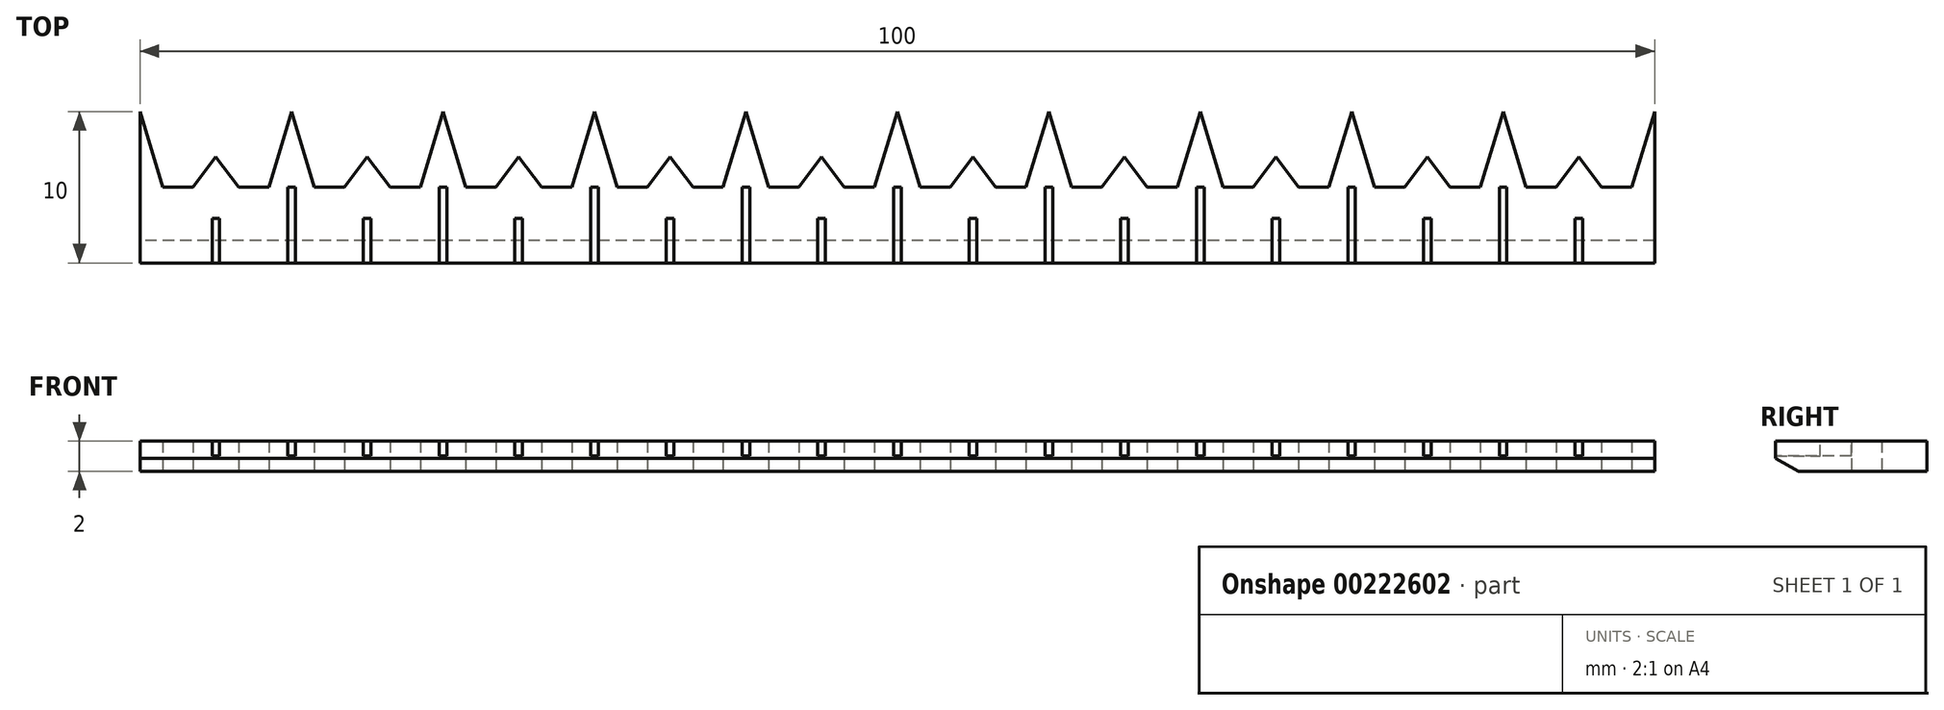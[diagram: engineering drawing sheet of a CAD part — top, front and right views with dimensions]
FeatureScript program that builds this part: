
annotation { "Feature Type Name" : "Feature", "Feature Type Description" : "" }
export const myFeature = defineFeature(function(context is Context, id is Id, definition is map)
    precondition{}
    {
        {
            var Q0;
            Q0=qCreatedBy(makeId("Top.planeOp"),FACE);
            var sketch = newSketch(context, id + "F0", { "sketchPlane" : qUnion([Q0])});
            skLineSegment(sketch, "E0.bottom", {"start": v(50, -2.5) * mm, "end": v(-50, -2.5) * mm});
            skLineSegment(sketch, "E0.top", {"start": v(50, 2.5) * mm, "end": v(-50, 2.5) * mm});
            skLineSegment(sketch, "E0.left", {"start": v(50, -2.5) * mm, "end": v(50, 2.5) * mm});
            skLineSegment(sketch, "E0.right", {"start": v(-50, -2.5) * mm, "end": v(-50, 2.5) * mm});
            skPoint(sketch, "E0.middle", {"position": v(0, 0) * mm});
            skLineSegment(sketch, "E1", {"start": v(-40, -2.5) * mm, "end": v(-40, 23.77) * mm, "construction": true});
            skLineSegment(sketch, "E2", {"start": v(-41.5, 2.5) * mm, "end": v(-40, 7.5) * mm});
            skLineSegment(sketch, "E3.MirrorCS", {"start": v(-38.5, 2.5) * mm, "end": v(-40, 7.5) * mm});
            skLineSegment(sketch, "E4.1.0.0", {"start": v(-31.5, 2.5) * mm, "end": v(-30, 7.5) * mm});
            skLineSegment(sketch, "E4.1.0.1", {"start": v(-28.5, 2.5) * mm, "end": v(-30, 7.5) * mm});
            skLineSegment(sketch, "E4.2.0.0", {"start": v(-21.5, 2.5) * mm, "end": v(-20, 7.5) * mm});
            skLineSegment(sketch, "E4.2.0.1", {"start": v(-18.5, 2.5) * mm, "end": v(-20, 7.5) * mm});
            skLineSegment(sketch, "E4.3.0.0", {"start": v(-11.5, 2.5) * mm, "end": v(-10, 7.5) * mm});
            skLineSegment(sketch, "E4.3.0.1", {"start": v(-8.5, 2.5) * mm, "end": v(-10, 7.5) * mm});
            skLineSegment(sketch, "E4.4.0.0", {"start": v(-1.5, 2.5) * mm, "end": v(0, 7.5) * mm});
            skLineSegment(sketch, "E4.4.0.1", {"start": v(1.5, 2.5) * mm, "end": v(0, 7.5) * mm});
            skLineSegment(sketch, "E4.5.0.0", {"start": v(8.5, 2.5) * mm, "end": v(10, 7.5) * mm});
            skLineSegment(sketch, "E4.5.0.1", {"start": v(11.5, 2.5) * mm, "end": v(10, 7.5) * mm});
            skLineSegment(sketch, "E4.6.0.0", {"start": v(18.5, 2.5) * mm, "end": v(20, 7.5) * mm});
            skLineSegment(sketch, "E4.6.0.1", {"start": v(21.5, 2.5) * mm, "end": v(20, 7.5) * mm});
            skLineSegment(sketch, "E4.7.0.0", {"start": v(28.5, 2.5) * mm, "end": v(30, 7.5) * mm});
            skLineSegment(sketch, "E4.7.0.1", {"start": v(31.5, 2.5) * mm, "end": v(30, 7.5) * mm});
            skLineSegment(sketch, "E4.8.0.0", {"start": v(38.5, 2.5) * mm, "end": v(40, 7.5) * mm});
            skLineSegment(sketch, "E4.8.0.1", {"start": v(41.5, 2.5) * mm, "end": v(40, 7.5) * mm});
            skLineSegment(sketch, "E4.direction1", {"start": v(-41.5, 2.5) * mm, "end": v(-31.5, 2.5) * mm, "construction": true});
            skLineSegment(sketch, "E5", {"start": v(-48.5, 2.5) * mm, "end": v(-50, 7.5) * mm});
            skLineSegment(sketch, "E6", {"start": v(-50, 7.5) * mm, "end": v(-50, 2.5) * mm});
            skLineSegment(sketch, "E7", {"start": v(48.5, 2.5) * mm, "end": v(50, 7.5) * mm});
            skLineSegment(sketch, "E8", {"start": v(-50, 2.5) * mm, "end": v(-48.5, 2.5) * mm});
            skLineSegment(sketch, "E9", {"start": v(48.5, 2.5) * mm, "end": v(50, 2.5) * mm});
            skLineSegment(sketch, "E10", {"start": v(50, 7.5) * mm, "end": v(50, 2.5) * mm});
            skLineSegment(sketch, "E11", {"start": v(-41.5, 2.5) * mm, "end": v(-40, 2.5) * mm});
            skLineSegment(sketch, "E12", {"start": v(-45, -2.5) * mm, "end": v(-45, 6.78) * mm, "construction": true});
            skLineSegment(sketch, "E13", {"start": v(-46.5, 2.5) * mm, "end": v(-45, 4.5) * mm});
            skLineSegment(sketch, "E14.MirrorCS", {"start": v(-43.5, 2.5) * mm, "end": v(-45, 4.5) * mm});
            skLineSegment(sketch, "E15", {"start": v(-46.5, 2.5) * mm, "end": v(-43.5, 2.5) * mm});
            skLineSegment(sketch, "E16", {"start": v(-41.5, 2.5) * mm, "end": v(-38.5, 2.5) * mm});
            skLineSegment(sketch, "E17.1.0.0", {"start": v(-33.5, 2.5) * mm, "end": v(-35, 4.5) * mm});
            skLineSegment(sketch, "E17.1.0.1", {"start": v(-36.5, 2.5) * mm, "end": v(-35, 4.5) * mm});
            skLineSegment(sketch, "E17.1.0.2", {"start": v(-36.5, 2.5) * mm, "end": v(-33.5, 2.5) * mm});
            skLineSegment(sketch, "E17.2.0.0", {"start": v(-23.5, 2.5) * mm, "end": v(-25, 4.5) * mm});
            skLineSegment(sketch, "E17.2.0.1", {"start": v(-26.5, 2.5) * mm, "end": v(-25, 4.5) * mm});
            skLineSegment(sketch, "E17.2.0.2", {"start": v(-26.5, 2.5) * mm, "end": v(-23.5, 2.5) * mm});
            skLineSegment(sketch, "E17.3.0.0", {"start": v(-13.5, 2.5) * mm, "end": v(-15, 4.5) * mm});
            skLineSegment(sketch, "E17.3.0.1", {"start": v(-16.5, 2.5) * mm, "end": v(-15, 4.5) * mm});
            skLineSegment(sketch, "E17.3.0.2", {"start": v(-16.5, 2.5) * mm, "end": v(-13.5, 2.5) * mm});
            skLineSegment(sketch, "E17.4.0.0", {"start": v(-3.5, 2.5) * mm, "end": v(-5, 4.5) * mm});
            skLineSegment(sketch, "E17.4.0.1", {"start": v(-6.5, 2.5) * mm, "end": v(-5, 4.5) * mm});
            skLineSegment(sketch, "E17.4.0.2", {"start": v(-6.5, 2.5) * mm, "end": v(-3.5, 2.5) * mm});
            skLineSegment(sketch, "E17.5.0.0", {"start": v(6.5, 2.5) * mm, "end": v(5, 4.5) * mm});
            skLineSegment(sketch, "E17.5.0.1", {"start": v(3.5, 2.5) * mm, "end": v(5, 4.5) * mm});
            skLineSegment(sketch, "E17.5.0.2", {"start": v(3.5, 2.5) * mm, "end": v(6.5, 2.5) * mm});
            skLineSegment(sketch, "E17.6.0.0", {"start": v(16.5, 2.5) * mm, "end": v(15, 4.5) * mm});
            skLineSegment(sketch, "E17.6.0.1", {"start": v(13.5, 2.5) * mm, "end": v(15, 4.5) * mm});
            skLineSegment(sketch, "E17.6.0.2", {"start": v(13.5, 2.5) * mm, "end": v(16.5, 2.5) * mm});
            skLineSegment(sketch, "E17.7.0.0", {"start": v(26.5, 2.5) * mm, "end": v(25, 4.5) * mm});
            skLineSegment(sketch, "E17.7.0.1", {"start": v(23.5, 2.5) * mm, "end": v(25, 4.5) * mm});
            skLineSegment(sketch, "E17.7.0.2", {"start": v(23.5, 2.5) * mm, "end": v(26.5, 2.5) * mm});
            skLineSegment(sketch, "E17.8.0.0", {"start": v(36.5, 2.5) * mm, "end": v(35, 4.5) * mm});
            skLineSegment(sketch, "E17.8.0.1", {"start": v(33.5, 2.5) * mm, "end": v(35, 4.5) * mm});
            skLineSegment(sketch, "E17.8.0.2", {"start": v(33.5, 2.5) * mm, "end": v(36.5, 2.5) * mm});
            skLineSegment(sketch, "E17.9.0.0", {"start": v(46.5, 2.5) * mm, "end": v(45, 4.5) * mm});
            skLineSegment(sketch, "E17.9.0.1", {"start": v(43.5, 2.5) * mm, "end": v(45, 4.5) * mm});
            skLineSegment(sketch, "E17.9.0.2", {"start": v(43.5, 2.5) * mm, "end": v(46.5, 2.5) * mm});
            skLineSegment(sketch, "E17.direction1", {"start": v(-46.5, 2.5) * mm, "end": v(-36.5, 2.5) * mm, "construction": true});
            skSolve(sketch);
        }
        {
            var Q0;
            Q0 = qSketchRegion(id + "F0", true);
            extrude(context, id + "F1", {"entities" : qUnion([Q0]), "depth" : 2 * mm});
        }
        {
            var Q0;
            Q0=makeQuery(id+"F1.opExtrude","CAP_EDGE",EDGE,{"disambiguationData":[OSD([sQuery(id+"F0.wireOp",EDGE,"E0.bottom")])],"isStart":true});
            chamfer(context, id + "F2", {"entities" : qUnion([Q0]), "chamferType" : ChamferType.OFFSET_ANGLE, "width" : 1.5 * mm, "oppositeDirection" : false, "angle" : 30 * degree, "tangentPropagation" : true});
        }
        {
            var Q0;
            Q0=makeQuery(id+"F1.opExtrude","CAP_FACE",FACE,{"disambiguationData":[OSD([sQuery(id+"F0.wireOp",EDGE,"E0.bottom"),sQuery(id+"F0.wireOp",EDGE,"E0.top"),sQuery(id+"F0.wireOp",EDGE,"E0.left"),sQuery(id+"F0.wireOp",EDGE,"E0.right"),sQuery(id+"F0.wireOp",EDGE,"E2"),sQuery(id+"F0.wireOp",EDGE,"E3.MirrorCS"),sQuery(id+"F0.wireOp",EDGE,"E4.1.0.0"),sQuery(id+"F0.wireOp",EDGE,"E4.1.0.1"),sQuery(id+"F0.wireOp",EDGE,"E4.2.0.0"),sQuery(id+"F0.wireOp",EDGE,"E4.2.0.1"),sQuery(id+"F0.wireOp",EDGE,"E4.3.0.0"),sQuery(id+"F0.wireOp",EDGE,"E4.3.0.1"),sQuery(id+"F0.wireOp",EDGE,"E4.4.0.0"),sQuery(id+"F0.wireOp",EDGE,"E4.4.0.1"),sQuery(id+"F0.wireOp",EDGE,"E4.5.0.0"),sQuery(id+"F0.wireOp",EDGE,"E4.5.0.1"),sQuery(id+"F0.wireOp",EDGE,"E4.6.0.0"),sQuery(id+"F0.wireOp",EDGE,"E4.6.0.1"),sQuery(id+"F0.wireOp",EDGE,"E4.7.0.0"),sQuery(id+"F0.wireOp",EDGE,"E4.7.0.1"),sQuery(id+"F0.wireOp",EDGE,"E4.8.0.0"),sQuery(id+"F0.wireOp",EDGE,"E4.8.0.1"),sQuery(id+"F0.wireOp",EDGE,"E5"),sQuery(id+"F0.wireOp",EDGE,"E6"),sQuery(id+"F0.wireOp",EDGE,"E7"),sQuery(id+"F0.wireOp",EDGE,"E10"),sQuery(id+"F0.wireOp",EDGE,"E13"),sQuery(id+"F0.wireOp",EDGE,"E14.MirrorCS"),sQuery(id+"F0.wireOp",EDGE,"E17.1.0.0"),sQuery(id+"F0.wireOp",EDGE,"E17.1.0.1"),sQuery(id+"F0.wireOp",EDGE,"E17.2.0.0"),sQuery(id+"F0.wireOp",EDGE,"E17.2.0.1"),sQuery(id+"F0.wireOp",EDGE,"E17.3.0.0"),sQuery(id+"F0.wireOp",EDGE,"E17.3.0.1"),sQuery(id+"F0.wireOp",EDGE,"E17.4.0.0"),sQuery(id+"F0.wireOp",EDGE,"E17.4.0.1"),sQuery(id+"F0.wireOp",EDGE,"E17.5.0.0"),sQuery(id+"F0.wireOp",EDGE,"E17.5.0.1"),sQuery(id+"F0.wireOp",EDGE,"E17.6.0.0"),sQuery(id+"F0.wireOp",EDGE,"E17.6.0.1"),sQuery(id+"F0.wireOp",EDGE,"E17.7.0.0"),sQuery(id+"F0.wireOp",EDGE,"E17.7.0.1"),sQuery(id+"F0.wireOp",EDGE,"E17.8.0.0"),sQuery(id+"F0.wireOp",EDGE,"E17.8.0.1"),sQuery(id+"F0.wireOp",EDGE,"E17.9.0.0"),sQuery(id+"F0.wireOp",EDGE,"E17.9.0.1")])],"isStart":false});
            var sketch = newSketch(context, id + "F3", { "sketchPlane" : qUnion([Q0])});
            skLineSegment(sketch, "E18.bottom", {"start": v(-39.75, 2.5) * mm, "end": v(-40.25, 2.5) * mm});
            skLineSegment(sketch, "E18.top", {"start": v(-39.75, -2.5) * mm, "end": v(-40.25, -2.5) * mm});
            skLineSegment(sketch, "E18.left", {"start": v(-39.75, 2.5) * mm, "end": v(-39.75, -2.5) * mm});
            skLineSegment(sketch, "E18.right", {"start": v(-40.25, 2.5) * mm, "end": v(-40.25, -2.5) * mm});
            skPoint(sketch, "E18.middle", {"position": v(-40, 0) * mm});
            skLineSegment(sketch, "E19.1.0.0", {"start": v(-29.75, 2.5) * mm, "end": v(-29.75, -2.5) * mm});
            skLineSegment(sketch, "E19.1.0.1", {"start": v(-30.25, 2.5) * mm, "end": v(-30.25, -2.5) * mm});
            skPoint(sketch, "E19.1.0.2", {"position": v(-30, 0) * mm});
            skLineSegment(sketch, "E19.1.0.3", {"start": v(-29.75, 2.5) * mm, "end": v(-30.25, 2.5) * mm});
            skLineSegment(sketch, "E19.1.0.4", {"start": v(-29.75, -2.5) * mm, "end": v(-30.25, -2.5) * mm});
            skLineSegment(sketch, "E19.2.0.0", {"start": v(-19.75, 2.5) * mm, "end": v(-19.75, -2.5) * mm});
            skLineSegment(sketch, "E19.2.0.1", {"start": v(-20.25, 2.5) * mm, "end": v(-20.25, -2.5) * mm});
            skPoint(sketch, "E19.2.0.2", {"position": v(-20, 0) * mm});
            skLineSegment(sketch, "E19.2.0.3", {"start": v(-19.75, 2.5) * mm, "end": v(-20.25, 2.5) * mm});
            skLineSegment(sketch, "E19.2.0.4", {"start": v(-19.75, -2.5) * mm, "end": v(-20.25, -2.5) * mm});
            skLineSegment(sketch, "E19.3.0.0", {"start": v(-9.75, 2.5) * mm, "end": v(-9.75, -2.5) * mm});
            skLineSegment(sketch, "E19.3.0.1", {"start": v(-10.25, 2.5) * mm, "end": v(-10.25, -2.5) * mm});
            skPoint(sketch, "E19.3.0.2", {"position": v(-10, 0) * mm});
            skLineSegment(sketch, "E19.3.0.3", {"start": v(-9.75, 2.5) * mm, "end": v(-10.25, 2.5) * mm});
            skLineSegment(sketch, "E19.3.0.4", {"start": v(-9.75, -2.5) * mm, "end": v(-10.25, -2.5) * mm});
            skLineSegment(sketch, "E19.4.0.0", {"start": v(0.25, 2.5) * mm, "end": v(0.25, -2.5) * mm});
            skLineSegment(sketch, "E19.4.0.1", {"start": v(-0.25, 2.5) * mm, "end": v(-0.25, -2.5) * mm});
            skPoint(sketch, "E19.4.0.2", {"position": v(0, 0) * mm});
            skLineSegment(sketch, "E19.4.0.3", {"start": v(0.25, 2.5) * mm, "end": v(-0.25, 2.5) * mm});
            skLineSegment(sketch, "E19.4.0.4", {"start": v(0.25, -2.5) * mm, "end": v(-0.25, -2.5) * mm});
            skLineSegment(sketch, "E19.5.0.0", {"start": v(10.25, 2.5) * mm, "end": v(10.25, -2.5) * mm});
            skLineSegment(sketch, "E19.5.0.1", {"start": v(9.75, 2.5) * mm, "end": v(9.75, -2.5) * mm});
            skPoint(sketch, "E19.5.0.2", {"position": v(10, 0) * mm});
            skLineSegment(sketch, "E19.5.0.3", {"start": v(10.25, 2.5) * mm, "end": v(9.75, 2.5) * mm});
            skLineSegment(sketch, "E19.5.0.4", {"start": v(10.25, -2.5) * mm, "end": v(9.75, -2.5) * mm});
            skLineSegment(sketch, "E19.6.0.0", {"start": v(20.25, 2.5) * mm, "end": v(20.25, -2.5) * mm});
            skLineSegment(sketch, "E19.6.0.1", {"start": v(19.75, 2.5) * mm, "end": v(19.75, -2.5) * mm});
            skPoint(sketch, "E19.6.0.2", {"position": v(20, 0) * mm});
            skLineSegment(sketch, "E19.6.0.3", {"start": v(20.25, 2.5) * mm, "end": v(19.75, 2.5) * mm});
            skLineSegment(sketch, "E19.6.0.4", {"start": v(20.25, -2.5) * mm, "end": v(19.75, -2.5) * mm});
            skLineSegment(sketch, "E19.7.0.0", {"start": v(30.25, 2.5) * mm, "end": v(30.25, -2.5) * mm});
            skLineSegment(sketch, "E19.7.0.1", {"start": v(29.75, 2.5) * mm, "end": v(29.75, -2.5) * mm});
            skPoint(sketch, "E19.7.0.2", {"position": v(30, 0) * mm});
            skLineSegment(sketch, "E19.7.0.3", {"start": v(30.25, 2.5) * mm, "end": v(29.75, 2.5) * mm});
            skLineSegment(sketch, "E19.7.0.4", {"start": v(30.25, -2.5) * mm, "end": v(29.75, -2.5) * mm});
            skLineSegment(sketch, "E19.8.0.0", {"start": v(40.25, 2.5) * mm, "end": v(40.25, -2.5) * mm});
            skLineSegment(sketch, "E19.8.0.1", {"start": v(39.75, 2.5) * mm, "end": v(39.75, -2.5) * mm});
            skPoint(sketch, "E19.8.0.2", {"position": v(40, 0) * mm});
            skLineSegment(sketch, "E19.8.0.3", {"start": v(40.25, 2.5) * mm, "end": v(39.75, 2.5) * mm});
            skLineSegment(sketch, "E19.8.0.4", {"start": v(40.25, -2.5) * mm, "end": v(39.75, -2.5) * mm});
            skLineSegment(sketch, "E19.direction1", {"start": v(-40.25, -2.5) * mm, "end": v(-30.25, -2.5) * mm, "construction": true});
            skLineSegment(sketch, "E20.bottom", {"start": v(-44.75, -2.5) * mm, "end": v(-45.25, -2.5) * mm});
            skLineSegment(sketch, "E20.top", {"start": v(-44.75, 0.45) * mm, "end": v(-45.25, 0.45) * mm});
            skLineSegment(sketch, "E20.left", {"start": v(-44.75, -2.5) * mm, "end": v(-44.75, 0.45) * mm});
            skLineSegment(sketch, "E20.right", {"start": v(-45.25, -2.5) * mm, "end": v(-45.25, 0.45) * mm});
            skPoint(sketch, "E20.middle", {"position": v(-45, -1.03) * mm});
            skLineSegment(sketch, "E21.1.0.0", {"start": v(-34.75, 0.45) * mm, "end": v(-35.25, 0.45) * mm});
            skLineSegment(sketch, "E21.1.0.1", {"start": v(-34.75, -2.5) * mm, "end": v(-34.75, 0.45) * mm});
            skPoint(sketch, "E21.1.0.2", {"position": v(-35, -1.03) * mm});
            skLineSegment(sketch, "E21.1.0.3", {"start": v(-34.75, -2.5) * mm, "end": v(-35.25, -2.5) * mm});
            skLineSegment(sketch, "E21.1.0.4", {"start": v(-35.25, -2.5) * mm, "end": v(-35.25, 0.45) * mm});
            skLineSegment(sketch, "E21.2.0.0", {"start": v(-24.75, 0.45) * mm, "end": v(-25.25, 0.45) * mm});
            skLineSegment(sketch, "E21.2.0.1", {"start": v(-24.75, -2.5) * mm, "end": v(-24.75, 0.45) * mm});
            skPoint(sketch, "E21.2.0.2", {"position": v(-25, -1.03) * mm});
            skLineSegment(sketch, "E21.2.0.3", {"start": v(-24.75, -2.5) * mm, "end": v(-25.25, -2.5) * mm});
            skLineSegment(sketch, "E21.2.0.4", {"start": v(-25.25, -2.5) * mm, "end": v(-25.25, 0.45) * mm});
            skLineSegment(sketch, "E21.3.0.0", {"start": v(-14.75, 0.45) * mm, "end": v(-15.25, 0.45) * mm});
            skLineSegment(sketch, "E21.3.0.1", {"start": v(-14.75, -2.5) * mm, "end": v(-14.75, 0.45) * mm});
            skPoint(sketch, "E21.3.0.2", {"position": v(-15, -1.03) * mm});
            skLineSegment(sketch, "E21.3.0.3", {"start": v(-14.75, -2.5) * mm, "end": v(-15.25, -2.5) * mm});
            skLineSegment(sketch, "E21.3.0.4", {"start": v(-15.25, -2.5) * mm, "end": v(-15.25, 0.45) * mm});
            skLineSegment(sketch, "E21.4.0.0", {"start": v(-4.75, 0.45) * mm, "end": v(-5.25, 0.45) * mm});
            skLineSegment(sketch, "E21.4.0.1", {"start": v(-4.75, -2.5) * mm, "end": v(-4.75, 0.45) * mm});
            skPoint(sketch, "E21.4.0.2", {"position": v(-5, -1.03) * mm});
            skLineSegment(sketch, "E21.4.0.3", {"start": v(-4.75, -2.5) * mm, "end": v(-5.25, -2.5) * mm});
            skLineSegment(sketch, "E21.4.0.4", {"start": v(-5.25, -2.5) * mm, "end": v(-5.25, 0.45) * mm});
            skLineSegment(sketch, "E21.5.0.0", {"start": v(5.25, 0.45) * mm, "end": v(4.75, 0.45) * mm});
            skLineSegment(sketch, "E21.5.0.1", {"start": v(5.25, -2.5) * mm, "end": v(5.25, 0.45) * mm});
            skPoint(sketch, "E21.5.0.2", {"position": v(5, -1.03) * mm});
            skLineSegment(sketch, "E21.5.0.3", {"start": v(5.25, -2.5) * mm, "end": v(4.75, -2.5) * mm});
            skLineSegment(sketch, "E21.5.0.4", {"start": v(4.75, -2.5) * mm, "end": v(4.75, 0.45) * mm});
            skLineSegment(sketch, "E21.6.0.0", {"start": v(15.25, 0.45) * mm, "end": v(14.75, 0.45) * mm});
            skLineSegment(sketch, "E21.6.0.1", {"start": v(15.25, -2.5) * mm, "end": v(15.25, 0.45) * mm});
            skPoint(sketch, "E21.6.0.2", {"position": v(15, -1.03) * mm});
            skLineSegment(sketch, "E21.6.0.3", {"start": v(15.25, -2.5) * mm, "end": v(14.75, -2.5) * mm});
            skLineSegment(sketch, "E21.6.0.4", {"start": v(14.75, -2.5) * mm, "end": v(14.75, 0.45) * mm});
            skLineSegment(sketch, "E21.7.0.0", {"start": v(25.25, 0.45) * mm, "end": v(24.75, 0.45) * mm});
            skLineSegment(sketch, "E21.7.0.1", {"start": v(25.25, -2.5) * mm, "end": v(25.25, 0.45) * mm});
            skPoint(sketch, "E21.7.0.2", {"position": v(25, -1.03) * mm});
            skLineSegment(sketch, "E21.7.0.3", {"start": v(25.25, -2.5) * mm, "end": v(24.75, -2.5) * mm});
            skLineSegment(sketch, "E21.7.0.4", {"start": v(24.75, -2.5) * mm, "end": v(24.75, 0.45) * mm});
            skLineSegment(sketch, "E21.8.0.0", {"start": v(35.25, 0.45) * mm, "end": v(34.75, 0.45) * mm});
            skLineSegment(sketch, "E21.8.0.1", {"start": v(35.25, -2.5) * mm, "end": v(35.25, 0.45) * mm});
            skPoint(sketch, "E21.8.0.2", {"position": v(35, -1.03) * mm});
            skLineSegment(sketch, "E21.8.0.3", {"start": v(35.25, -2.5) * mm, "end": v(34.75, -2.5) * mm});
            skLineSegment(sketch, "E21.8.0.4", {"start": v(34.75, -2.5) * mm, "end": v(34.75, 0.45) * mm});
            skLineSegment(sketch, "E21.9.0.0", {"start": v(45.25, 0.45) * mm, "end": v(44.75, 0.45) * mm});
            skLineSegment(sketch, "E21.9.0.1", {"start": v(45.25, -2.5) * mm, "end": v(45.25, 0.45) * mm});
            skPoint(sketch, "E21.9.0.2", {"position": v(45, -1.03) * mm});
            skLineSegment(sketch, "E21.9.0.3", {"start": v(45.25, -2.5) * mm, "end": v(44.75, -2.5) * mm});
            skLineSegment(sketch, "E21.9.0.4", {"start": v(44.75, -2.5) * mm, "end": v(44.75, 0.45) * mm});
            skLineSegment(sketch, "E21.direction1", {"start": v(-45.25, -2.5) * mm, "end": v(-35.25, -2.5) * mm, "construction": true});
            skSolve(sketch);
        }
        {
            var Q0;
            Q0 = qSketchRegion(id + "F3", true);
            extrude(context, id + "F4", {"entities" : qUnion([Q0]), "operationType" : NewBodyOperationType.REMOVE, "oppositeDirection" : true, "depth" : 1 * mm});
        }
    });
